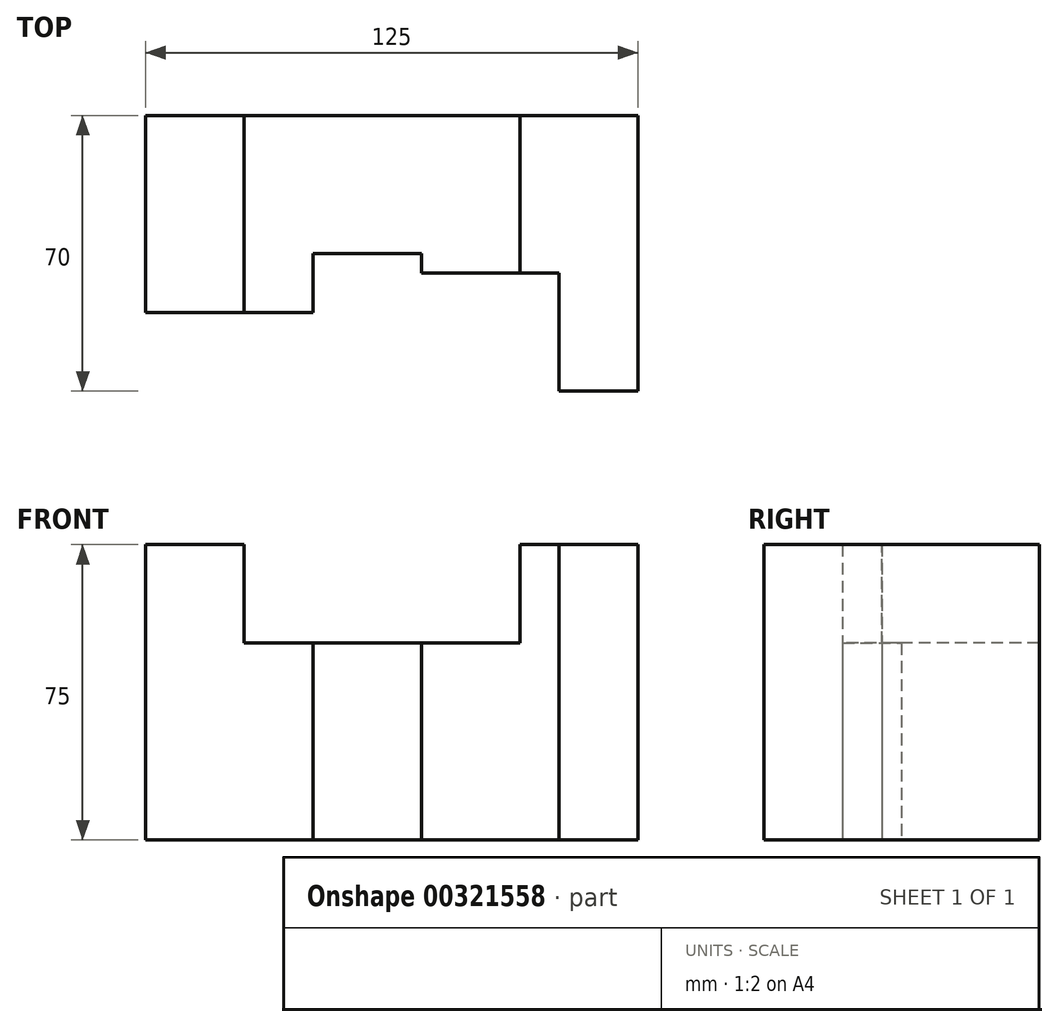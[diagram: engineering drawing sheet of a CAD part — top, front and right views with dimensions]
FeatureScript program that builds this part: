
annotation { "Feature Type Name" : "Feature", "Feature Type Description" : "" }
export const myFeature = defineFeature(function(context is Context, id is Id, definition is map)
    precondition{}
    {
        {
            var Q0;
            Q0=qCreatedBy(makeId("Front.planeOp"),FACE);
            var sketch = newSketch(context, id + "F0", { "sketchPlane" : qUnion([Q0])});
            skLineSegment(sketch, "E0", {"start": v(0, 0) * mm, "end": v(0, 75) * mm});
            skLineSegment(sketch, "E1", {"start": v(0, 75) * mm, "end": v(125, 75) * mm});
            skLineSegment(sketch, "E2", {"start": v(125, 75) * mm, "end": v(125, 0) * mm});
            skLineSegment(sketch, "E3", {"start": v(125, 0) * mm, "end": v(0, 0) * mm});
            skSolve(sketch);
        }
        {
            var Q0;
            Q0 = qSketchRegion(id + "F0", true);
            extrude(context, id + "F1", {"entities" : qUnion([Q0]), "depth" : (14 * 5) * mm});
        }
        {
            var Q0;
            Q0=makeQuery(id+"F1.opExtrude","CAP_FACE",FACE,{"disambiguationData":[OSD([sQuery(id+"F0.wireOp",EDGE,"E0"),sQuery(id+"F0.wireOp",EDGE,"E1"),sQuery(id+"F0.wireOp",EDGE,"E2"),sQuery(id+"F0.wireOp",EDGE,"E3")])],"isStart":false});
            var sketch = newSketch(context, id + "F2", { "sketchPlane" : qUnion([Q0])});
            skLineSegment(sketch, "E4", {"start": v(25, 75) * mm, "end": v(25, 50) * mm});
            skLineSegment(sketch, "E5", {"start": v(25, 50) * mm, "end": v(95, 50) * mm});
            skLineSegment(sketch, "E6", {"start": v(95, 50) * mm, "end": v(95, 75) * mm});
            skLineSegment(sketch, "E7", {"start": v(95, 75) * mm, "end": v(25, 75) * mm});
            skSolve(sketch);
        }
        {
            var Q0;
            Q0=makeQuery(id+"F2.imprint","IMPRINT",FACE,{"disambiguationData":[TD([[makeQuery(id+"F2.imprint","IMPRINT",EDGE,{"derivedFrom":sQuery(id+"F2.wireOp",EDGE,"E4")}),1.0]])]});
            extrude(context, id + "F3", {"entities" : qUnion([Q0]), "operationType" : NewBodyOperationType.REMOVE, "endBound" : BoundingType.THROUGH_ALL, "oppositeDirection" : true, "depth" : 25 * mm});
        }
        {
            var Q0;
            Q0=qCreatedBy(makeId("Top.planeOp"),FACE);
            var sketch = newSketch(context, id + "F4", { "sketchPlane" : qUnion([Q0])});
            skLineSegment(sketch, "E8", {"start": v(0, -70) * mm, "end": v(0, -50) * mm});
            skLineSegment(sketch, "E9", {"start": v(0, -50) * mm, "end": v(42.5, -50) * mm});
            skLineSegment(sketch, "E10", {"start": v(42.5, -50) * mm, "end": v(42.5, -35) * mm});
            skLineSegment(sketch, "E11", {"start": v(42.5, -35) * mm, "end": v(70, -35) * mm});
            skLineSegment(sketch, "E12", {"start": v(70, -70) * mm, "end": v(0, -70) * mm});
            skLineSegment(sketch, "E13", {"start": v(70, -35) * mm, "end": v(70, -40) * mm});
            skLineSegment(sketch, "E14", {"start": v(105, -40) * mm, "end": v(105, -70) * mm});
            skLineSegment(sketch, "E15", {"start": v(105, -70) * mm, "end": v(70, -70) * mm});
            skLineSegment(sketch, "E16", {"start": v(70, -40) * mm, "end": v(105, -40) * mm});
            skSolve(sketch);
        }
        {
            var Q0;
            Q0 = qSketchRegion(id + "F4", true);
            extrude(context, id + "F5", {"entities" : qUnion([Q0]), "operationType" : NewBodyOperationType.REMOVE, "endBound" : BoundingType.THROUGH_ALL, "depth" : 25 * mm});
        }
    });
